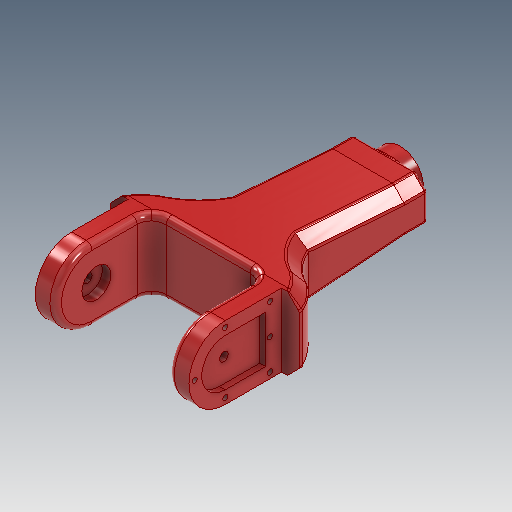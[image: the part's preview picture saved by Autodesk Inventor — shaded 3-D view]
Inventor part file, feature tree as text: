
AUTODESK INVENTOR PART (.ipt)
format: ipt  version: 2020.3 (Build 243373010, 373A)  size: 1,020,416 bytes
history: native  units: mm
features: extrude x11, sketch x8, fillet x6, projected_geometry x4, mirror x3, hole x3, chamfer x2, plane x1, delete_face x1, pattern_linear x1
ambient origin geometry x8: Origin, YZ Plane, XZ Plane, XY Plane, X Axis, Y Axis, Z Axis, Center Point
bodies: Solid1 (feature_tree)
feature tree (40):
  extrude  "Extrusion1"  Depth=305.0mm
  extrude  "Extrusion2"  Depth=470.0mm
  extrude  "Extrusion3"  Depth=50.0mm
  extrude  "Extrusion4"  Depth=125.0mm TaperAngle=0.0deg
  extrude  "Extrusion5"  Depth=15.0mm
  fillet  "Fillet1"  Radius=25.0mm
  chamfer  "Chamfer1"  Distance=15.0mm
  fillet  "Fillet2"  Radius=65.0mm
  sketch  "Sketch9"  dims[d11=165.0mm d12=470.0mm]
  plane  "Work Plane1"
  extrude  "Extrusion8"  Depth=125.0mm
  extrude  "Extrusion9"  Depth=20.0mm
  extrude  "Extrusion10"  Depth=10.0mm
  chamfer  "Chamfer2"  Distance=145.0mm
  delete_face  "Delete Face1"
  extrude  "Extrusion11"  Depth=10.0mm
  mirror  "Mirror3"
  hole  "Hole1"  [1 undecoded]
  mirror  "Mirror4"
  extrude  "Extrusion12"  Depth=10.0mm
  mirror  "Mirror6"
  sketch  "Sketch23"  dims[d33=85.0mm d34=125.0mm]
  fillet  "Fillet3"  Radius=62.5mm
  fillet  "Fillet4"  Radius=62.5mm
  fillet  "Fillet5"  Radius=20.0mm
  fillet  "Fillet6"  Radius=10.0mm
  extrude  "Extrusion13"  TaperAngle=0.0deg  [1 undecoded]
  sketch  "Sketch29"  dims[d35=20.0mm d36=20.0mm]
  hole  "Hole7"  [1 undecoded]
  pattern_linear  "Rectangular Pattern4"  Spacing1=25.0mm  [1 undecoded]
  hole  "Hole8"  [1 undecoded]
  sketch  "Sketch2"  dims[d5=194.0mm d9=305.0mm]
  projected_geometry  "Projected Loop1"
  sketch  "Sketch11"  dims[d13=50.0mm d14=50.0mm]
  projected_geometry  "Projected Loop2"
  sketch  "Sketch15"  dims[d15=65.0mm d17=125.0mm d18=0.0mm]
  sketch  "Sketch21"  dims[d23=50.0mm d24=15.0mm d25=25.0mm d26=0.0mm d27=15.0mm d28=0.0mm d30=65.0mm]
  projected_geometry  "Projected Loop6"
  projected_geometry  "Projected Loop8"
  sketch  "Sketch30"  dims[d37=0.0mm d38=0.0mm d39=324.0mm d40=145.0mm d41=100.0mm d43=115.0mm d44=110.0mm d45=62.5mm d46=0.0mm d47=62.5mm d48=20.0mm d49=2.0mm d50=45.0deg d51=10.0mm d58=0.0mm d59=80.0mm d60=25.0mm d61=0.0mm d62=65.0mm d63=250.0mm d64=0.0mm d67=50.0mm d68=50.0mm d69=0.0mm d70=2.0mm d71=2.0mm d72=45.0deg d74=324.0mm d75=324.0mm d76=65.0mm d77=72.5mm d78=72.5mm d79=89.5mm d80=30.0mm d81=0.0mm d82=8.917468mm d83=20.0mm d84=4.0mm d85=2.0mm d86=90.0deg d87=25.1mm d88=0.0mm d90=17.5mm d91=17.5mm d121=22.0mm d122=10.0mm d123=0.0mm d124=20.0mm d125=5.0mm d126=5.0mm d127=5.0mm d128=5.0mm d142=105.0mm d143=8.574719mm d144=8.574719mm d145=87.850561mm d148=105.0mm d149=8.574719mm d150=8.574719mm d151=87.850561mm d169=43.925281mm d170=43.925281mm d171=221.210734mm d172=235.0mm d173=10.0mm d174=0.0mm d175=10.917mm d176=24.0mm d177=3.023mm d178=2.0mm d179=14.3117mm d180=29.1mm d181=20.594885mm d182=50.0mm d184=50.0mm d185=10.917mm d186=24.0mm d187=3.023mm d188=2.0mm d189=14.3117mm d190=29.1mm d191=20.594885mm]
note: 5 required parameter values undecoded (feature->parameter linkage not recoverable at this tier; creation-order binding heuristic only, values carry confidence <= 0.55)
